# Revit family: EURS_63_LF_FB_StyliD Evo Compact ST770X_PHI
name_source: partatom
category: Lighting Fixtures
revit_build: Autodesk Revit 2016 (Build: 20161004_0715(x64)
units: mm (PartAtom-declared; Revit-internal decimal feet)

## family parameters
Cut with Voids When Loaded = No
Host = Face
Light Source = No
Part Type = Normal
Room Calculation Point = No
Round Connector Dimension = Use Diameter
Shared = Yes

## types (1)
- Type catalog
    12NC = 12NC CODE
    Apparent Load = 18 VA
    BIM Library - URL = http://www.lighting.philips.com
    Ceiling thickness = 13 mm
    Constraint XY = 90.00°
    Constraint XZ = 0.00°
    Content modified date = DATE
    Content version = 1.0
    Default Elevation = 0 mm  [stored 0 ft]
    Description = StyliD Evo Compact
    Diameter = 90 mm  [stored 0.295276 ft]
    EOC = EOC CODE
    ETIM code = EC001744
    ETIM code URL = https://prod.etim-international.com
    Fixture code = FIXTURE CODE
    Height = 230 mm  [stored 0.754593 ft]
    Lamp = LAMP NAME
    Last IES update = DATE
    Length = 90 mm  [stored 0.295276 ft]
    Light source = 2 mm  [stored 0.00656168 ft]
    Manufacturer = Philips
    Model = ST770X
    Order code = ORDER CODE
    Product catalog - URL = WEBPAGE MODEL
    Rim height = 60 mm  [stored 0.19685 ft]
    Rotation XY = 90.00°
    Rotation XZ = 0.00°
    Type Comments = Track Mount
    URL = http://www.lighting.philips.com
    Voltage (V) = 230 V
    Width = 380 mm

note: [stored X ft] marks values corroborated as IEEE doubles in the binary element streams (Revit-internal decimal feet)

## geometry (parser evidence)
native form markers: Blend x3, Sweep x30
no freeform markers — native parametric forms only
